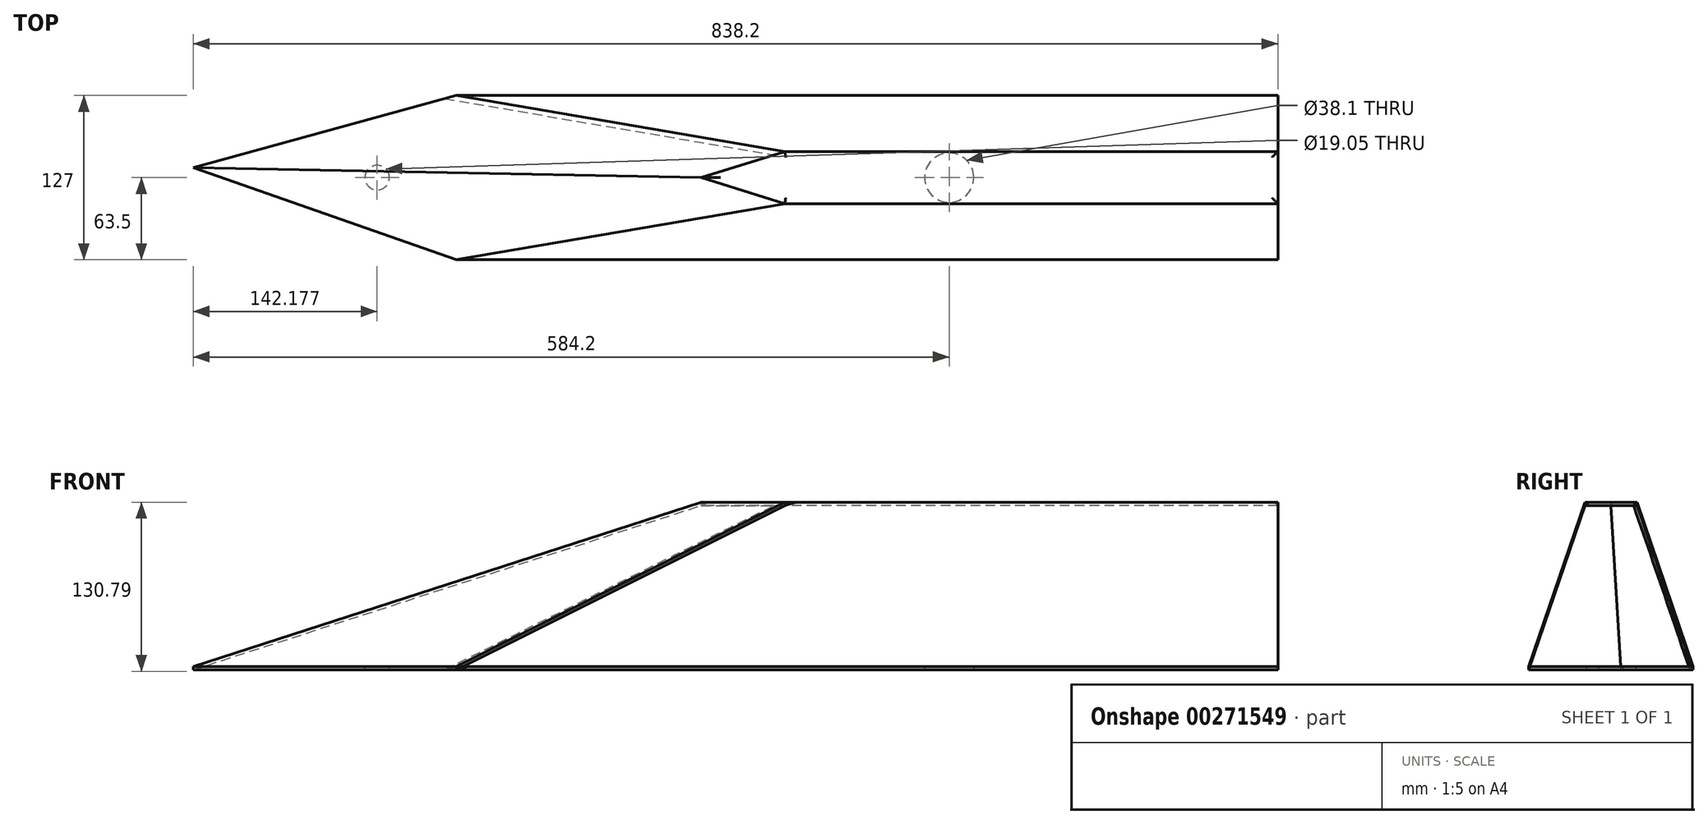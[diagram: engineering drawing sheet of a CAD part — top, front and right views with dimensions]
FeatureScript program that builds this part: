
annotation { "Feature Type Name" : "Feature", "Feature Type Description" : "" }
export const myFeature = defineFeature(function(context is Context, id is Id, definition is map)
    precondition{}
    {
        {
            var Q0;
            Q0=qCreatedBy(makeId("Top.planeOp"),FACE);
            var sketch = newSketch(context, id + "F0", { "sketchPlane" : qUnion([Q0])});
            skLineSegment(sketch, "E0.bottom", {"start": v(-63.5, 63.5) * mm, "end": v(571.5, 63.5) * mm});
            skLineSegment(sketch, "E0.top", {"start": v(-63.5, -63.5) * mm, "end": v(571.5, -63.5) * mm});
            skLineSegment(sketch, "E0.left", {"start": v(-63.5, 63.5) * mm, "end": v(-63.5, -63.5) * mm});
            skLineSegment(sketch, "E0.right", {"start": v(571.5, 63.5) * mm, "end": v(571.5, -63.5) * mm});
            skPoint(sketch, "E0.middle", {"position": v(254, 0) * mm});
            skLineSegment(sketch, "E1", {"start": v(-63.5, 63.5) * mm, "end": v(-266.7, 7.78) * mm});
            skLineSegment(sketch, "E2", {"start": v(-266.7, 7.78) * mm, "end": v(-63.5, -63.5) * mm});
            skCircle(sketch, "E3", {"center": v(317.5, 0) * mm, "radius": 19.05 * mm});
            skCircle(sketch, "E4", {"center": v(-124.52, 0) * mm, "radius": 9.53 * mm});
            skPoint(sketch, "E4.centerSnap0", {"position": v(-63.5, 0) * mm});
            skLineSegment(sketch, "E5.bottom", {"start": v(-124.52, 46.77) * mm, "end": v(-124.52, 46.77) * mm});
            skLineSegment(sketch, "E5.top", {"start": v(-124.52, -46.77) * mm, "end": v(-124.52, -46.77) * mm});
            skSolve(sketch);
        }
        {
            var Q0;
            Q0=qCreatedBy(makeId("Top.planeOp"),FACE);
            cPlane(context, id + "F1", {"entities" : qUnion([Q0]), "cplaneType" : CPlaneType.OFFSET, "offset" : 127 * mm, "width" : 152.4 * mm, "height" : 152.4 * mm});
        }
        {
            var Q0;
            Q0=qCreatedBy(id+"F1.planeOp",FACE);
            var sketch = newSketch(context, id + "F2", { "sketchPlane" : qUnion([Q0])});
            skLineSegment(sketch, "E6", {"start": v(571.5, 20.17) * mm, "end": v(571.5, -20.17) * mm});
            skLineSegment(sketch, "E7.bottom", {"start": v(571.5, 20.17) * mm, "end": v(190.5, 20.17) * mm});
            skLineSegment(sketch, "E7.top", {"start": v(571.5, -20.17) * mm, "end": v(190.5, -20.17) * mm});
            skLineSegment(sketch, "E7.right", {"start": v(190.5, 20.17) * mm, "end": v(190.5, -20.17) * mm});
            skLineSegment(sketch, "E8", {"start": v(190.5, 20.17) * mm, "end": v(125.88, 0) * mm});
            skLineSegment(sketch, "E9", {"start": v(125.88, 0) * mm, "end": v(190.5, -20.17) * mm});
            skSolve(sketch);
        }
        {
            var Q0;
            Q0 = qSketchRegion(id + "F0", true);
            var Q1;
            Q1 = qSketchRegion(id + "F2", true);
            extrude(context, id + "F3", {"entities" : qUnion([Q0, Q1]), "depth" : 2.54 * mm});
        }
        {
            var Q0;
            Q0=makeQuery(id+"F3.opExtrude","SWEPT_FACE",FACE,{"disambiguationData":[OSD([sQuery(id+"F0.wireOp",EDGE,"E0.top")])]});
            var Q1;
            Q1=makeQuery(id+"F3.opExtrude","SWEPT_FACE",FACE,{"disambiguationData":[OSD([sQuery(id+"F2.wireOp",EDGE,"E7.top")])]});
            loft(context, id + "F4", {"sheetProfilesArray" : [{ "sheetProfileEntities" : qUnion([Q0]) }, { "sheetProfileEntities" : qUnion([Q1]) }]});
        }
        {
            var Q0;
            Q0=makeQuery(id+"F3.opExtrude","SWEPT_FACE",FACE,{"disambiguationData":[OSD([sQuery(id+"F0.wireOp",EDGE,"E2")])]});
            var Q1;
            Q1=makeQuery(id+"F3.opExtrude","SWEPT_FACE",FACE,{"disambiguationData":[OSD([sQuery(id+"F2.wireOp",EDGE,"E9")])]});
            loft(context, id + "F5", {"sheetProfilesArray" : [{ "sheetProfileEntities" : qUnion([Q0]) }, { "sheetProfileEntities" : qUnion([Q1]) }]});
        }
        {
            var Q0;
            Q0=makeQuery(id+"F3.opExtrude","SWEPT_FACE",FACE,{"disambiguationData":[OSD([sQuery(id+"F0.wireOp",EDGE,"E1")])]});
            var Q1;
            Q1=makeQuery(id+"F3.opExtrude","SWEPT_FACE",FACE,{"disambiguationData":[OSD([sQuery(id+"F2.wireOp",EDGE,"E8")])]});
            loft(context, id + "F6", {"sheetProfilesArray" : [{ "sheetProfileEntities" : qUnion([Q0]) }, { "sheetProfileEntities" : qUnion([Q1]) }]});
        }
        {
            var Q0;
            Q0=makeQuery(id+"F3.opExtrude","SWEPT_FACE",FACE,{"disambiguationData":[OSD([sQuery(id+"F2.wireOp",EDGE,"E7.bottom")])]});
            var Q1;
            Q1=makeQuery(id+"F3.opExtrude","SWEPT_FACE",FACE,{"disambiguationData":[OSD([sQuery(id+"F0.wireOp",EDGE,"E0.bottom")])]});
            loft(context, id + "F7", {"sheetProfilesArray" : [{ "sheetProfileEntities" : qUnion([Q0]) }, { "sheetProfileEntities" : qUnion([Q1]) }]});
        }
        {
            var Q0;
            Q0=makeQuery(id+"F3.opExtrude","CAP_EDGE",EDGE,{"disambiguationData":[OSD([sQuery(id+"F2.wireOp",EDGE,"E7.bottom")])],"isStart":false});
            var Q1;
            Q1=makeQuery(id+"F3.opExtrude","CAP_EDGE",EDGE,{"disambiguationData":[OSD([sQuery(id+"F2.wireOp",EDGE,"E8")])],"isStart":false});
            var Q2;
            Q2=makeQuery(id+"F3.opExtrude","CAP_EDGE",EDGE,{"disambiguationData":[OSD([sQuery(id+"F2.wireOp",EDGE,"E7.top")])],"isStart":false});
            var Q3;
            Q3=makeQuery(id+"F3.opExtrude","CAP_EDGE",EDGE,{"disambiguationData":[OSD([sQuery(id+"F2.wireOp",EDGE,"E9")])],"isStart":false});
            var Q4;
            Q4=makeQuery(id+"F3.opExtrude","CAP_EDGE",EDGE,{"disambiguationData":[OSD([sQuery(id+"F2.wireOp",EDGE,"E6")])],"isStart":false});
            var Q5;
            {var subQ0=sQuery(id+"F2.wireOp",EDGE,"E8");var subQ1=sQuery(id+"F2.wireOp",EDGE,"E7.right");var subQ2=sQuery(id+"F2.wireOp",EDGE,"E7.bottom");var subQ3=sQuery(id+"F0.wireOp",EDGE,"E1");var subQ4=sQuery(id+"F0.wireOp",EDGE,"E0.left");var subQ5=sQuery(id+"F0.wireOp",EDGE,"E0.bottom");Q5=makeQuery(id+"F6.opLoft","SWEPT_EDGE",EDGE,{"disambiguationData":[OSD([subQ5,subQ4,subQ3,subQ2,subQ1,subQ0]),TDD([makeQuery(id+"F3.opExtrude","CAP_VERTEX",VERTEX,{"disambiguationData":[OSD([subQ5,subQ4,subQ3])],"isStart":true}),makeQuery(id+"F3.opExtrude","CAP_VERTEX",VERTEX,{"disambiguationData":[OSD([subQ2,subQ1,subQ0])],"isStart":true})])]});}
            var Q6;
            {var subQ0=sQuery(id+"F2.wireOp",EDGE,"E9");var subQ1=sQuery(id+"F2.wireOp",EDGE,"E7.right");var subQ2=sQuery(id+"F2.wireOp",EDGE,"E7.top");var subQ3=sQuery(id+"F0.wireOp",EDGE,"E2");var subQ4=sQuery(id+"F0.wireOp",EDGE,"E0.left");var subQ5=sQuery(id+"F0.wireOp",EDGE,"E0.top");Q6=makeQuery(id+"F4.opLoft","SWEPT_EDGE",EDGE,{"disambiguationData":[OSD([subQ5,subQ4,subQ3,subQ2,subQ1,subQ0]),TDD([makeQuery(id+"F3.opExtrude","CAP_VERTEX",VERTEX,{"disambiguationData":[OSD([subQ5,subQ4,subQ3])],"isStart":false}),makeQuery(id+"F3.opExtrude","CAP_VERTEX",VERTEX,{"disambiguationData":[OSD([subQ2,subQ1,subQ0])],"isStart":false})])]});}
            fillet(context, id + "F8", {"entities" : qUnion([Q0, Q1, Q2, Q3, Q4, Q5, Q6]), "radius" : 5.08 * mm, "tangentPropagation" : true, "allowEdgeOverflow" : false});
        }
    });
